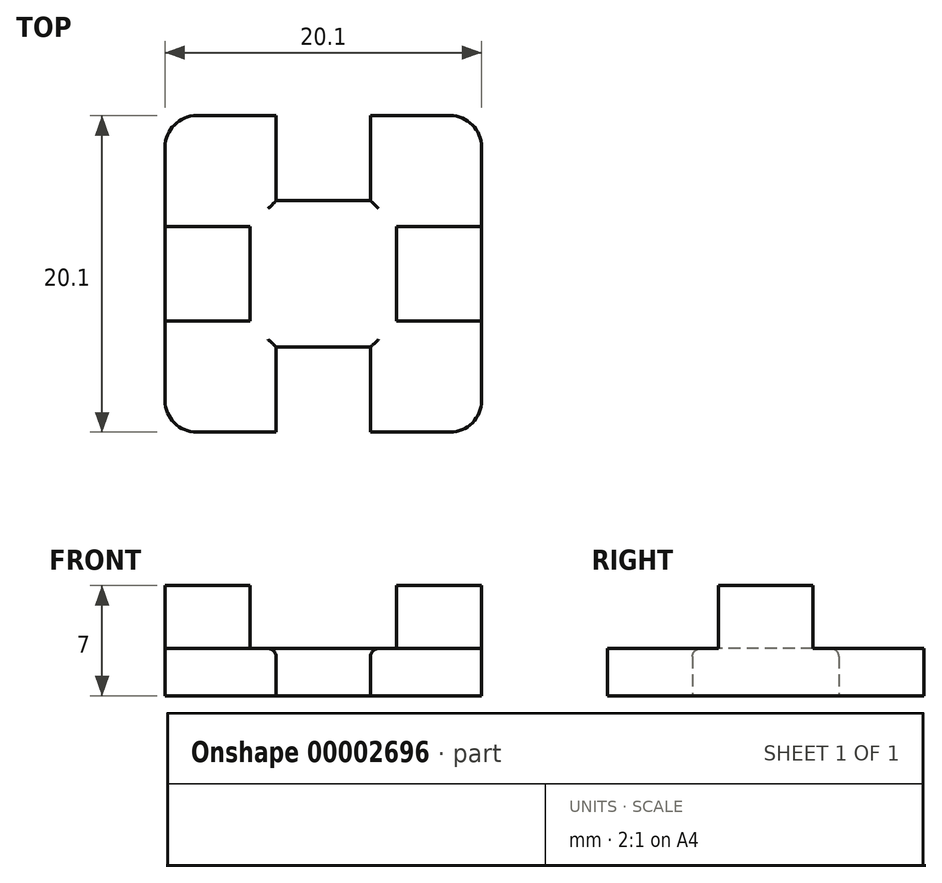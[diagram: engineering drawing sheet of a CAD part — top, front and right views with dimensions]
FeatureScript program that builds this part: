
annotation { "Feature Type Name" : "Feature", "Feature Type Description" : "" }
export const myFeature = defineFeature(function(context is Context, id is Id, definition is map)
    precondition{}
    {
        {
            var Q0;
            Q0=qCreatedBy(makeId("Top.planeOp"),FACE);
            var sketch = newSketch(context, id + "F0", { "sketchPlane" : qUnion([Q0])});
            skLineSegment(sketch, "E0.bottom", {"start": v(-8, 0) * mm, "end": v(12.1, 0) * mm});
            skLineSegment(sketch, "E0.top", {"start": v(-8, 20.1) * mm, "end": v(12.1, 20.1) * mm});
            skLineSegment(sketch, "E0.left", {"start": v(-8, 0) * mm, "end": v(-8, 20.1) * mm});
            skLineSegment(sketch, "E0.right", {"start": v(12.1, 0) * mm, "end": v(12.1, 20.1) * mm});
            skPoint(sketch, "E1", {"position": v(2.05, 20.1) * mm});
            skPoint(sketch, "E2", {"position": v(12.1, 10.05) * mm});
            skLineSegment(sketch, "E3.bottom", {"start": v(-0.95, 20.1) * mm, "end": v(5.05, 20.1) * mm});
            skLineSegment(sketch, "E3.top", {"start": v(-0.95, 14.7) * mm, "end": v(5.05, 14.7) * mm});
            skLineSegment(sketch, "E3.left", {"start": v(-0.95, 20.1) * mm, "end": v(-0.95, 14.7) * mm});
            skLineSegment(sketch, "E3.right", {"start": v(5.05, 20.1) * mm, "end": v(5.05, 14.7) * mm});
            skLineSegment(sketch, "E4.bottom", {"start": v(-0.95, 0) * mm, "end": v(5.05, 0) * mm});
            skLineSegment(sketch, "E4.top", {"start": v(-0.95, 5.4) * mm, "end": v(5.05, 5.4) * mm});
            skLineSegment(sketch, "E4.left", {"start": v(-0.95, 0) * mm, "end": v(-0.95, 5.4) * mm});
            skLineSegment(sketch, "E4.right", {"start": v(5.05, 0) * mm, "end": v(5.05, 5.4) * mm});
            skLineSegment(sketch, "E5.bottom", {"start": v(-8, 13.05) * mm, "end": v(-2.6, 13.05) * mm});
            skLineSegment(sketch, "E5.top", {"start": v(-8, 7.05) * mm, "end": v(-2.6, 7.05) * mm});
            skLineSegment(sketch, "E5.left", {"start": v(-8, 13.05) * mm, "end": v(-8, 7.05) * mm});
            skLineSegment(sketch, "E5.right", {"start": v(-2.6, 13.05) * mm, "end": v(-2.6, 7.05) * mm});
            skLineSegment(sketch, "E6.bottom", {"start": v(12.1, 13.05) * mm, "end": v(6.7, 13.05) * mm});
            skLineSegment(sketch, "E6.top", {"start": v(12.1, 7.05) * mm, "end": v(6.7, 7.05) * mm});
            skLineSegment(sketch, "E6.left", {"start": v(12.1, 13.05) * mm, "end": v(12.1, 7.05) * mm});
            skLineSegment(sketch, "E6.right", {"start": v(6.7, 13.05) * mm, "end": v(6.7, 7.05) * mm});
            skPoint(sketch, "E7", {"position": v(2.05, 14.7) * mm});
            skPoint(sketch, "E8", {"position": v(6.7, 10.05) * mm});
            skSolve(sketch);
        }
        {
            var Q0;
            Q0=makeQuery(id+"F0.imprint","IMPRINT",FACE,{"disambiguationData":[TD([[makeQuery(id+"F0.imprint","IMPRINT",EDGE,{"derivedFrom":sQuery(id+"F0.wireOp",EDGE,"E3.top")}),-1.0]])]});
            extrude(context, id + "F1", {"entities" : qUnion([Q0]), "depth" : 3 * mm});
        }
        {
            var Q0;
            Q0=makeQuery(id+"F0.imprint","IMPRINT",FACE,{"disambiguationData":[TD([[makeQuery(id+"F0.imprint","IMPRINT",EDGE,{"derivedFrom":sQuery(id+"F0.wireOp",EDGE,"E3.bottom")}),-1.0]])]});
            var Q1;
            Q1=makeQuery(id+"F0.imprint","IMPRINT",FACE,{"disambiguationData":[TD([[makeQuery(id+"F0.imprint","IMPRINT",EDGE,{"derivedFrom":sQuery(id+"F0.wireOp",EDGE,"E5.bottom")}),-1.0]])]});
            var Q2;
            Q2=makeQuery(id+"F0.imprint","IMPRINT",FACE,{"disambiguationData":[TD([[makeQuery(id+"F0.imprint","IMPRINT",EDGE,{"derivedFrom":sQuery(id+"F0.wireOp",EDGE,"E4.bottom")}),1.0]])]});
            var Q3;
            Q3=makeQuery(id+"F0.imprint","IMPRINT",FACE,{"disambiguationData":[TD([[makeQuery(id+"F0.imprint","IMPRINT",EDGE,{"derivedFrom":sQuery(id+"F0.wireOp",EDGE,"E6.bottom")}),1.0]])]});
            extrude(context, id + "F2", {"entities" : qUnion([Q0, Q1, Q2, Q3]), "operationType" : NewBodyOperationType.ADD, "depth" : 7 * mm});
        }
        {
            var Q0;
            Q0=makeQuery(id+"F1.opExtrude","SWEPT_EDGE",EDGE,{"disambiguationData":[OSD([sQuery(id+"F0.wireOp",EDGE,"E0.bottom"),sQuery(id+"F0.wireOp",EDGE,"E0.left")])]});
            var Q1;
            Q1=makeQuery(id+"F1.opExtrude","SWEPT_EDGE",EDGE,{"disambiguationData":[OSD([sQuery(id+"F0.wireOp",EDGE,"E0.bottom"),sQuery(id+"F0.wireOp",EDGE,"E0.right")])]});
            var Q2;
            Q2=makeQuery(id+"F1.opExtrude","SWEPT_EDGE",EDGE,{"disambiguationData":[OSD([sQuery(id+"F0.wireOp",EDGE,"E0.top"),sQuery(id+"F0.wireOp",EDGE,"E0.right")])]});
            var Q3;
            Q3=makeQuery(id+"F1.opExtrude","SWEPT_EDGE",EDGE,{"disambiguationData":[OSD([sQuery(id+"F0.wireOp",EDGE,"E0.top"),sQuery(id+"F0.wireOp",EDGE,"E0.left")])]});
            fillet(context, id + "F3", {"entities" : qUnion([Q0, Q1, Q2, Q3]), "radius" : 2 * mm, "tangentPropagation" : true, "allowEdgeOverflow" : false});
        }
        {
            var Q0;
            Q0=makeQuery(id+"F1.opExtrude","CAP_EDGE",EDGE,{"disambiguationData":[OSD([sQuery(id+"F0.wireOp",EDGE,"E3.right")])],"isStart":false});
            var Q1;
            Q1=makeQuery(id+"F1.opExtrude","CAP_EDGE",EDGE,{"disambiguationData":[OSD([sQuery(id+"F0.wireOp",EDGE,"E6.bottom")])],"isStart":false});
            var Q2;
            Q2=makeQuery(id+"F1.opExtrude","CAP_EDGE",EDGE,{"disambiguationData":[OSD([sQuery(id+"F0.wireOp",EDGE,"E3.top")])],"isStart":false});
            var Q3;
            Q3=makeQuery(id+"F1.opExtrude","CAP_EDGE",EDGE,{"disambiguationData":[OSD([sQuery(id+"F0.wireOp",EDGE,"E6.right")])],"isStart":false});
            var Q4;
            Q4=makeQuery(id+"F1.opExtrude","CAP_EDGE",EDGE,{"disambiguationData":[OSD([sQuery(id+"F0.wireOp",EDGE,"E5.right")])],"isStart":false});
            var Q5;
            Q5=makeQuery(id+"F1.opExtrude","CAP_EDGE",EDGE,{"disambiguationData":[OSD([sQuery(id+"F0.wireOp",EDGE,"E6.top")])],"isStart":false});
            var Q6;
            Q6=makeQuery(id+"F1.opExtrude","CAP_EDGE",EDGE,{"disambiguationData":[OSD([sQuery(id+"F0.wireOp",EDGE,"E4.left")])],"isStart":false});
            var Q7;
            Q7=makeQuery(id+"F1.opExtrude","CAP_EDGE",EDGE,{"disambiguationData":[OSD([sQuery(id+"F0.wireOp",EDGE,"E5.top")])],"isStart":false});
            var Q8;
            Q8=makeQuery(id+"F1.opExtrude","CAP_EDGE",EDGE,{"disambiguationData":[OSD([sQuery(id+"F0.wireOp",EDGE,"E4.right")])],"isStart":false});
            var Q9;
            Q9=makeQuery(id+"F1.opExtrude","CAP_EDGE",EDGE,{"disambiguationData":[OSD([sQuery(id+"F0.wireOp",EDGE,"E4.top")])],"isStart":false});
            var Q10;
            Q10=makeQuery(id+"F1.opExtrude","CAP_EDGE",EDGE,{"disambiguationData":[OSD([sQuery(id+"F0.wireOp",EDGE,"E5.bottom")])],"isStart":false});
            var Q11;
            Q11=makeQuery(id+"F1.opExtrude","CAP_EDGE",EDGE,{"disambiguationData":[OSD([sQuery(id+"F0.wireOp",EDGE,"E3.left")])],"isStart":false});
            fillet(context, id + "F4", {"entities" : qUnion([Q0, Q1, Q2, Q3, Q4, Q5, Q6, Q7, Q8, Q9, Q10, Q11]), "radius" : 0.5 * mm, "tangentPropagation" : true, "allowEdgeOverflow" : false});
        }
    });
